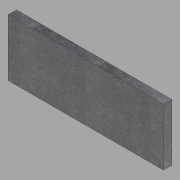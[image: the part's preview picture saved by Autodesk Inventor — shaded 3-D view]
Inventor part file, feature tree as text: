
AUTODESK INVENTOR PART (.ipt)
format: ipt  version: 2022.1 (Build 261234020, 234B)  size: 100,352 bytes
history: native  units: in
note: dims shown in document units (in); Inventor stores cm internally (conversion verified against a paired STEP export)
features: extrude x1, sketch x1
ambient origin geometry x8: Origin, YZ Plane, XZ Plane, XY Plane, X Axis, Y Axis, Z Axis, Center Point
bodies: Solid1 (feature_tree)
feature tree (2):
  extrude  "Extrusion1"  Depth=42.0in
  sketch  "Sketch1"  dims[d0=114.0in d1=42.0in d2=6.0in d3=0.0in]
